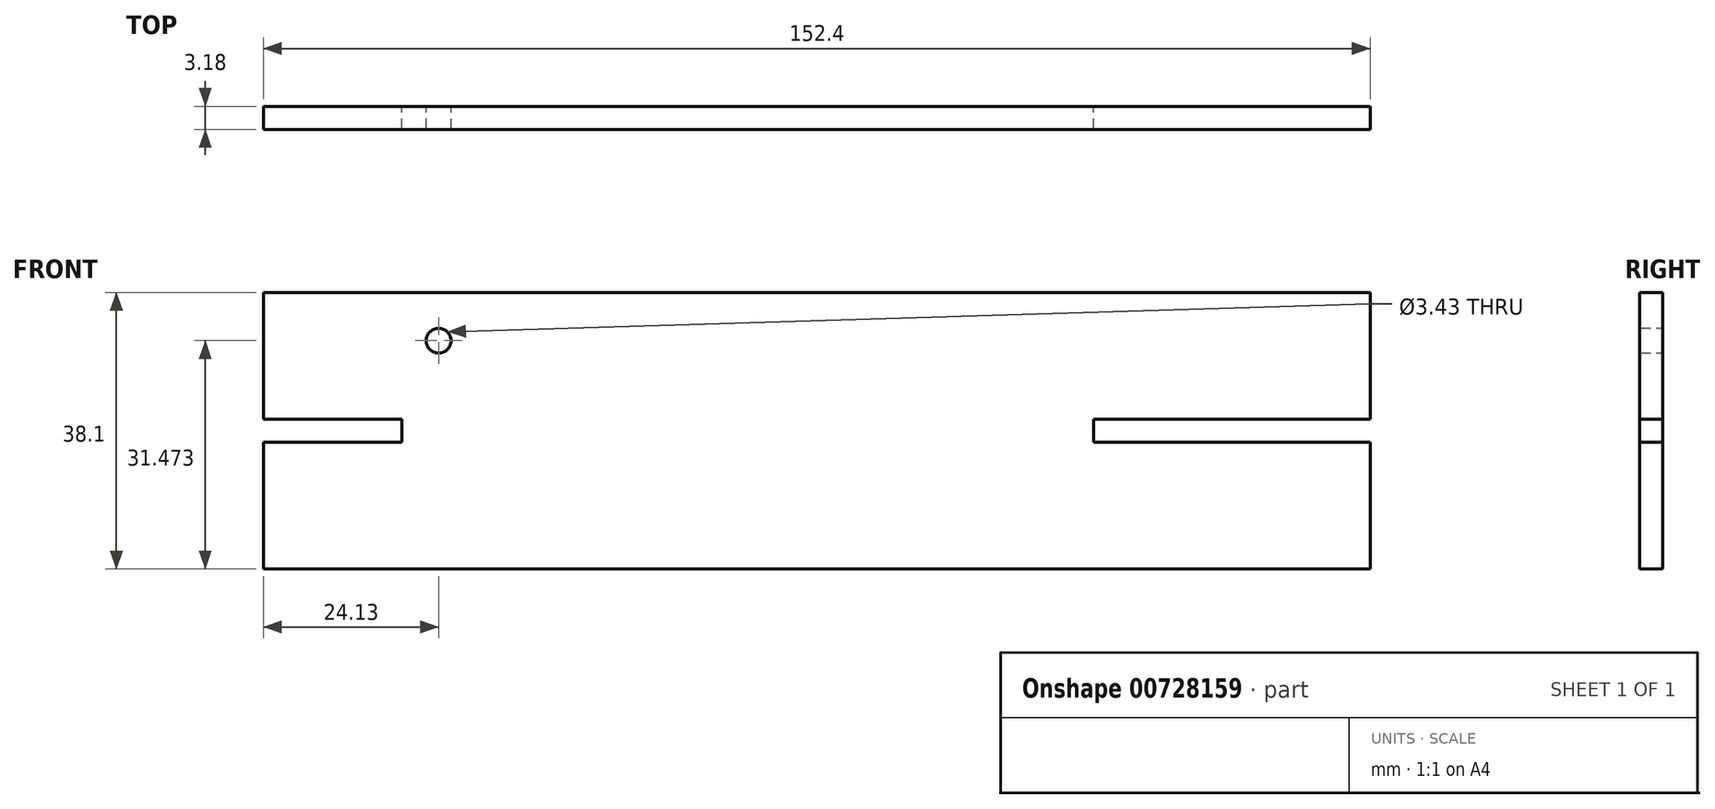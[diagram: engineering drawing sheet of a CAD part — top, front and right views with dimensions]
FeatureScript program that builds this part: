
annotation { "Feature Type Name" : "Feature", "Feature Type Description" : "" }
export const myFeature = defineFeature(function(context is Context, id is Id, definition is map)
    precondition{}
    {
        {
            var Q0;
            Q0=qCreatedBy(makeId("Front.planeOp"),FACE);
            var sketch = newSketch(context, id + "F0", { "sketchPlane" : qUnion([Q0])});
            skLineSegment(sketch, "E0", {"start": v(-79.28, 17.46) * mm, "end": v(73.12, 17.46) * mm});
            skLineSegment(sketch, "E1", {"start": v(73.12, 17.46) * mm, "end": v(73.12, -20.64) * mm});
            skLineSegment(sketch, "E2", {"start": v(-79.28, 17.46) * mm, "end": v(-79.28, -20.64) * mm});
            skLineSegment(sketch, "E3", {"start": v(73.12, -20.64) * mm, "end": v(-79.28, -20.64) * mm});
            skLineSegment(sketch, "E4", {"start": v(-79.28, -1.59) * mm, "end": v(73.12, -1.59) * mm});
            skCircle(sketch, "E5", {"center": v(-55.15, 10.83) * mm, "radius": 1.71 * mm});
            skLineSegment(sketch, "E6", {"start": v(-79.28, 0) * mm, "end": v(-60.23, 0) * mm});
            skLineSegment(sketch, "E7.MirrorCS", {"start": v(-79.28, -3.18) * mm, "end": v(-60.23, -3.17) * mm});
            skLineSegment(sketch, "E8", {"start": v(-60.23, 0) * mm, "end": v(-60.23, -3.17) * mm});
            skLineSegment(sketch, "E9.MirrorCS", {"start": v(73.12, 0) * mm, "end": v(35.02, 0) * mm});
            skLineSegment(sketch, "E10.MirrorCS", {"start": v(73.12, -3.17) * mm, "end": v(47.72, -3.17) * mm});
            skLineSegment(sketch, "E11.MirrorCS", {"start": v(73.12, -1.59) * mm, "end": v(-79.28, -1.59) * mm});
            skLineSegment(sketch, "E12.MirrorCS", {"start": v(47.72, 0) * mm, "end": v(47.72, -3.17) * mm});
            skLineSegment(sketch, "E13.MirrorCS", {"start": v(73.12, -3.17) * mm, "end": v(35.02, -3.17) * mm});
            skLineSegment(sketch, "E14", {"start": v(35.02, 0) * mm, "end": v(35.02, -3.17) * mm});
            skSolve(sketch);
        }
        {
            var Q0;
            {var subQ1=sQuery(id+"F0.wireOp",EDGE,"E0");Q0=makeQuery(id+"F0.imprint","IMPRINT",FACE,{"disambiguationData":[TD([[makeQuery(id+"F0.imprint","IMPRINT",EDGE,{"derivedFrom":subQ1}),-1.0]])]});}
            var Q1;
            {var subQ5=sQuery(id+"F0.wireOp",EDGE,"E3");Q1=makeQuery(id+"F0.imprint","IMPRINT",FACE,{"disambiguationData":[TD([[makeQuery(id+"F0.imprint","IMPRINT",EDGE,{"derivedFrom":subQ5}),-1.0]])]});}
            extrude(context, id + "F1", {"entities" : qUnion([Q0, Q1]), "depth" : 3.17 * mm, "offsetDistance" : 25.4 * mm});
        }
    });
